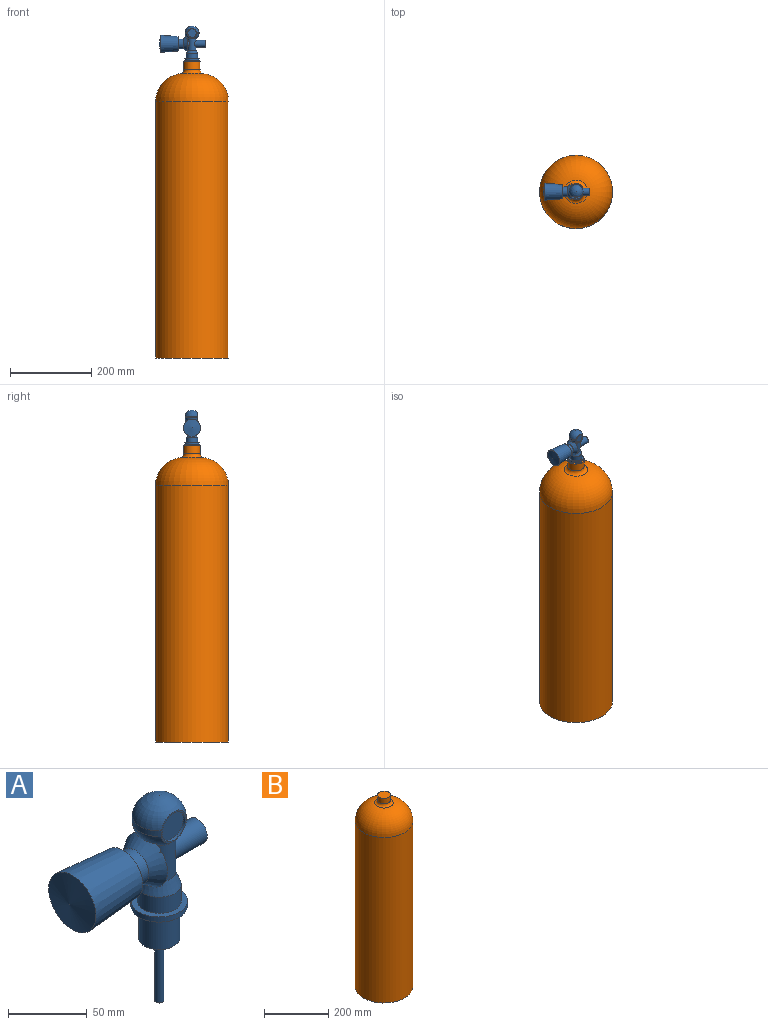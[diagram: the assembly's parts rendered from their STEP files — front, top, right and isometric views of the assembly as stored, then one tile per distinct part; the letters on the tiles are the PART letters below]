
ASSEMBLY  parts=2 mates=1
PART A: 27 faces, bbox 115.1x42.4x159 mm
  f0: revolved ~34.34x34.34mm, area 2295.3mm2, adj f1,f4,f14,f15,f24
  f1: cylinder r=17.21mm len=34.43mm, axis (0,0,-1), area 364.5mm2, adj f0,f2,f24
  f2: revolved ~34.43x34.43mm, area 1472.8mm2, adj f1,f24
  f3: cone r=14.05mm half-angle=20.4deg, axis (0,0,-1), area 785.9mm2, adj f4,f12,f14,f15
  f4: cylinder r=10.5mm len=28.09mm, axis (0,0,-1), area 1280.7mm2, adj f0,f3,f16,f18
  f5: plane 5.79x5.79mm, normal (0,0,-1), area 26.3mm2, adj f6
  f6: cylinder r=2.89mm len=48.66mm, axis (0,0,-1), area 884.6mm2, adj f5,f7
  f7: plane 26.18x26.18mm, normal (0,0,-1), area 512mm2, adj f6,f8
  f8: cylinder r=13.09mm len=26.18mm, axis (0,0,-1), area 2045.6mm2, adj f7,f9
  f9: plane 36.07x36.07mm, normal (0,0,-1), area 483.4mm2, adj f8,f10
  f10: cylinder r=18.03mm len=36.07mm, axis (0,0,-1), area 456.3mm2, adj f9,f11
  f11: plane 36.07x36.07mm, normal (0,0,1), area 401.6mm2, adj f10,f12
  f12: cylinder r=14.05mm len=28.1mm, axis (0,0,-1), area 1104.6mm2, adj f3,f11
  f13: cylinder r=12.34mm len=24.68mm, axis (1,0,0), area 838.3mm2, adj f14,f19
  f14: cone r=12.34mm half-angle=33.5deg, axis (1,0,0), area 1135.8mm2, adj f0,f3,f13,f15,f22,f23
  f15: cone r=18.97mm half-angle=84.8deg, axis (-1,0,0), area 808.4mm2, adj f0,f3,f14,f16,f22,f23
  f16: cylinder r=8.96mm len=17.93mm, axis (1,0,0), area 139.1mm2, adj f4,f15
  f17: plane 17.93x17.93mm, normal (1,0,0), area 252.4mm2, adj f18
  f18: cylinder r=8.96mm len=28.71mm, axis (1,0,0), area 1463.9mm2, adj f4,f17
  f19: plane 35.39x35.39mm, normal (1,0,0), area 505.5mm2, adj f13,f20
  f20: cone r=21.19mm half-angle=4.4deg, axis (-1,0,0), area 5595.2mm2, adj f19,f21
  f21: cone r=0mm half-angle=82.4deg, axis (1,0,0), area 1423.6mm2, adj f20
  f22: plane 1.74x1.1mm, normal (0,-1,0), area 0.9mm2, adj f14,f15,f23
  f23: cylinder r=19.38mm len=1.53mm, axis (0,-1,0), area 1mm2, adj f14,f15,f22
  f24: plane 23.01x22.57mm, normal (0,-1,0), area 73.2mm2, adj f0,f1,f2,f25
  f25: cylinder r=10.42mm len=20.84mm, axis (0,-1,0), area 124.4mm2, adj f24,f26
  f26: plane 20.84x20.84mm, normal (0,-1,0), area 341mm2, adj f25
PART B: 6 faces, bbox 180x180x732 mm
  f0: plane 180x180mm, normal (0,0,-1), area 25446.9mm2, adj f1
  f1: cylinder r=90mm len=632mm, axis (0,0,-1), area 357387.6mm2, adj f0,f2
  f2: torus R=20mm, axis (0,0,-1), area 43261.1mm2, adj f1,f3
  f3: torus R=30mm, axis (0,0,-1), area 2101.3mm2, adj f2,f4
  f4: cylinder r=20mm len=40mm, axis (0,0,-1), area 2592.1mm2, adj f3,f5
  f5: plane 40x40mm, normal (0,0,1), area 1256.6mm2, adj f4
PLACE A t=(-763.61,292.08,-557.29)mm
PLACE B t=(-603.09,292.08,-416.97)mm
MATE slider A.f1 <-> B.f1  axis (0,0,-1) through (-170.16,292.08,295.54)mm
